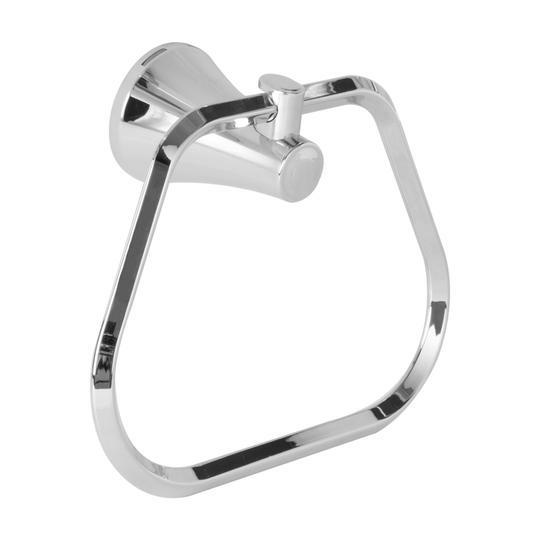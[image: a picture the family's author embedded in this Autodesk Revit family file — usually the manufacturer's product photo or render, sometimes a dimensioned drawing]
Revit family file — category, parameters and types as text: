
# Revit family: BL-2504-11 TOALLERO ARO CONTEMPRA
name_source: partatom
category: Plumbing Fixtures
revit_build: Autodesk Revit 2018 (Build: 20170223_1515(x64)
units: mm (PartAtom-declared; Revit-internal decimal feet)

## family parameters
Cut with Voids When Loaded = No
Host = Face
OmniClass Number = 23.31.11.00
Part Type = Normal
Room Calculation Point = No
Round Connector Dimension = Use Diameter
Shared = No

## types (1)
- BL-2504-11
    Alto gancho = 133 mm  [stored 0.436352 ft]
    Alto soporte = 70 mm
    Ancho gancho = 173 mm  [stored 0.567585 ft]
    CW Connection = Yes
    Default Elevation = 0 mm  [stored 0 ft]
    Description = Toallero
    Diametro base = 50 mm  [stored 0.164042 ft]
    HW Connection = Yes
    Link Ficha Tecnica = http://infotecnica.gricol.com
    Manufacturer = Gricol
    Model = BL-2504-11
    Plastico ABS cromado = Plastico - ABS Cromado
    Product Name = TOALLERO ARO CONTEMPRA
    Type Image = TOALLERO ARO CONTEMPRA.jpg
    URL = https://www.gricol.com
    Vent Connection = No
    Waste Connection = No

note: [stored X ft] marks values corroborated as IEEE doubles in the binary element streams (Revit-internal decimal feet)

## geometry (parser evidence)
native form markers: Blend x2, Sweep x3
no freeform markers — native parametric forms only
